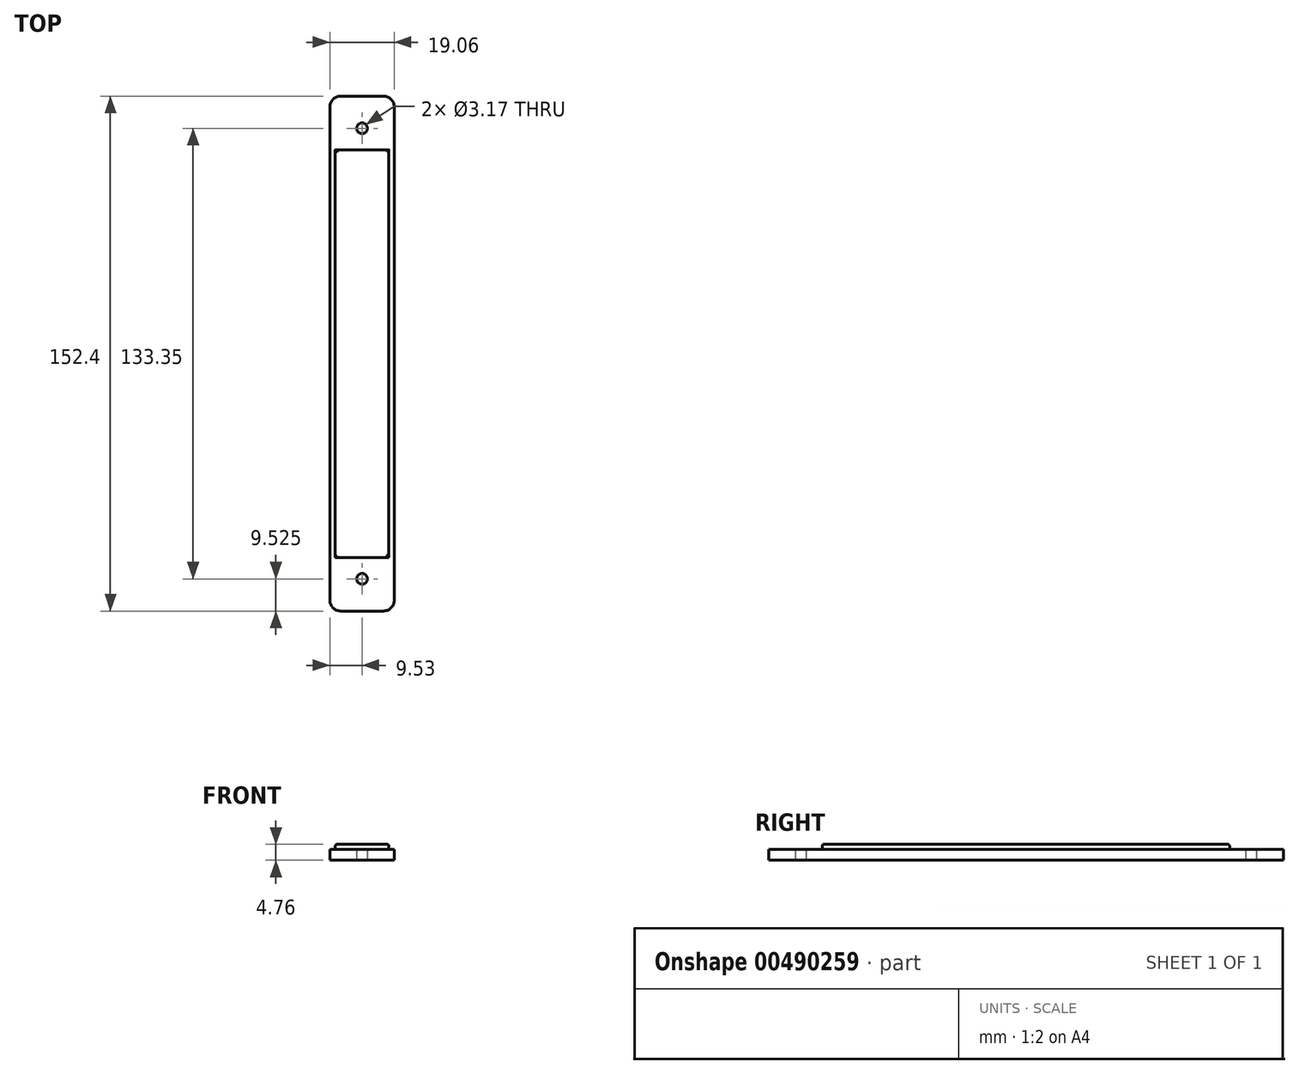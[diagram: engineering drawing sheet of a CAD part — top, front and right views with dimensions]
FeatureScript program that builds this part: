
annotation { "Feature Type Name" : "Feature", "Feature Type Description" : "" }
export const myFeature = defineFeature(function(context is Context, id is Id, definition is map)
    precondition{}
    {
        {
            var Q0;
            Q0=qCreatedBy(makeId("Top.planeOp"),FACE);
            var sketch = newSketch(context, id + "F0", { "sketchPlane" : qUnion([Q0])});
            skLineSegment(sketch, "E0.bottom", {"start": v(-6.35, 76.2) * mm, "end": v(6.35, 76.2) * mm});
            skLineSegment(sketch, "E0.top", {"start": v(-6.35, -76.2) * mm, "end": v(6.35, -76.2) * mm});
            skLineSegment(sketch, "E0.left", {"start": v(-9.52, 73.03) * mm, "end": v(-9.53, -73.03) * mm});
            skLineSegment(sketch, "E0.right", {"start": v(9.53, 73.03) * mm, "end": v(9.52, -73.03) * mm});
            skPoint(sketch, "E0.middle", {"position": v(0, 0) * mm});
            skPoint(sketch, "E1", {"position": v(0, 66.67) * mm});
            skPoint(sketch, "E2.MirrorP", {"position": v(0, -66.67) * mm});
            skPoint(sketch, "E3.visualSharp", {"position": v(-9.52, 76.2) * mm});
            skArc(sketch, "E3.filletArc", {"start": v(-6.35, 76.2) * mm, "mid": v(-8.6, 75.27) * mm, "end": v(-9.52, 73.03) * mm});
            skPoint(sketch, "E4.visualSharp", {"position": v(9.53, 76.2) * mm});
            skArc(sketch, "E4.filletArc", {"start": v(9.53, 73.03) * mm, "mid": v(8.6, 75.27) * mm, "end": v(6.35, 76.2) * mm});
            skPoint(sketch, "E5.visualSharp", {"position": v(9.52, -76.2) * mm});
            skArc(sketch, "E5.filletArc", {"start": v(6.35, -76.2) * mm, "mid": v(8.6, -75.27) * mm, "end": v(9.52, -73.03) * mm});
            skPoint(sketch, "E6.visualSharp", {"position": v(-9.53, -76.2) * mm});
            skArc(sketch, "E6.filletArc", {"start": v(-9.53, -73.03) * mm, "mid": v(-8.6, -75.27) * mm, "end": v(-6.35, -76.2) * mm});
            skSolve(sketch);
        }
        {
            var Q0;
            Q0=makeQuery(id+"F0.imprint","IMPRINT",FACE,{"disambiguationData":[TD([[makeQuery(id+"F0.imprint","IMPRINT",EDGE,{"derivedFrom":sQuery(id+"F0.wireOp",EDGE,"E0.bottom")}),-1.0]])]});
            extrude(context, id + "F1", {"entities" : qUnion([Q0]), "depth" : 3.17 * mm});
        }
        {
            var Q0;
            Q0=sQuery(id+"F0.wireOp",VERTEX,"E2.MirrorP");
            var Q1;
            Q1=sQuery(id+"F0.wireOp",VERTEX,"E1");
            var Q2;
            Q2=makeQuery(id+"F1.opExtrude","SWEPT_BODY",BODY,{"disambiguationData":[OSD([sQuery(id+"F0.wireOp",EDGE,"E0.bottom"),sQuery(id+"F0.wireOp",EDGE,"E0.top"),sQuery(id+"F0.wireOp",EDGE,"E0.left"),sQuery(id+"F0.wireOp",EDGE,"E0.right")])]});
            hole(context, id + "F2", {"style" : HoleStyle.SIMPLE, "endStyle" : HoleEndStyle.THROUGH, "oppositeDirection" : true, "holeDiameter" : 3.17 * mm, "isTappedThrough" : true, "tappedDepth" : 12.7 * mm, "tapClearance" : 3, "locations" : qUnion([Q0, Q1]), "scope" : qUnion([Q2])});
        }
        {
            var Q0;
            Q0=makeQuery(id+"F1.opExtrude","CAP_FACE",FACE,{"disambiguationData":[OSD([sQuery(id+"F0.wireOp",EDGE,"E0.bottom"),sQuery(id+"F0.wireOp",EDGE,"E0.top"),sQuery(id+"F0.wireOp",EDGE,"E0.left"),sQuery(id+"F0.wireOp",EDGE,"E0.right"),sQuery(id+"F0.wireOp",EDGE,"E3.filletArc"),sQuery(id+"F0.wireOp",EDGE,"E4.filletArc"),sQuery(id+"F0.wireOp",EDGE,"E5.filletArc"),sQuery(id+"F0.wireOp",EDGE,"E6.filletArc")])],"isStart":false});
            var sketch = newSketch(context, id + "F3", { "sketchPlane" : qUnion([Q0])});
            skPoint(sketch, "E7.middle", {"position": v(0, 0) * mm});
            skLineSegment(sketch, "E8.bottom", {"start": v(-7.94, 60.32) * mm, "end": v(7.94, 60.32) * mm});
            skLineSegment(sketch, "E8.top", {"start": v(-7.94, -60.32) * mm, "end": v(7.94, -60.32) * mm});
            skLineSegment(sketch, "E8.left", {"start": v(-7.94, 60.32) * mm, "end": v(-7.94, -60.32) * mm});
            skLineSegment(sketch, "E8.right", {"start": v(7.94, 60.32) * mm, "end": v(7.94, -60.32) * mm});
            skSolve(sketch);
        }
        {
            var Q0;
            Q0=makeQuery(id+"F3.imprint","IMPRINT",FACE,{"disambiguationData":[TD([[makeQuery(id+"F3.imprint","IMPRINT",EDGE,{"derivedFrom":sQuery(id+"F3.wireOp",EDGE,"E7.bottom")}),-1.0]])]});
            var Q1;
            Q1=makeQuery(id+"F3.imprint","IMPRINT",FACE,{"disambiguationData":[TD([[makeQuery(id+"F3.imprint","IMPRINT",EDGE,{"derivedFrom":sQuery(id+"F3.wireOp",EDGE,"E8.bottom")}),-1.0]])]});
            extrude(context, id + "F4", {"entities" : qUnion([Q0, Q1]), "operationType" : NewBodyOperationType.ADD, "depth" : 1.59 * mm});
        }
        {
            var Q0;
            Q0=makeQuery(id+"F4.opExtrude","CAP_EDGE",EDGE,{"disambiguationData":[OSD([sQuery(id+"F3.wireOp",EDGE,"E8.top")])],"isStart":false});
            var Q1;
            Q1=makeQuery(id+"F4.opExtrude","CAP_EDGE",EDGE,{"disambiguationData":[OSD([sQuery(id+"F3.wireOp",EDGE,"E8.right")])],"isStart":false});
            var Q2;
            Q2=makeQuery(id+"F4.opExtrude","CAP_EDGE",EDGE,{"disambiguationData":[OSD([sQuery(id+"F3.wireOp",EDGE,"E8.left")])],"isStart":false});
            var Q3;
            Q3=makeQuery(id+"F4.opExtrude","CAP_EDGE",EDGE,{"disambiguationData":[OSD([sQuery(id+"F3.wireOp",EDGE,"E8.bottom")])],"isStart":false});
            fillet(context, id + "F5", {"entities" : qUnion([Q0, Q1, Q2, Q3]), "radius" : 0.64 * mm, "tangentPropagation" : true, "allowEdgeOverflow" : false});
        }
    });
